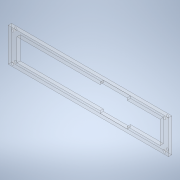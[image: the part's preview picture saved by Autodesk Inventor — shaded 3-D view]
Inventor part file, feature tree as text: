
AUTODESK INVENTOR PART (.ipt)
format: ipt  version: 2021 (Build 250183000, 183)  size: 140,800 bytes
history: native  units: mm
features: extrude x1, sketch x1
ambient origin geometry x8: Origin, YZ Plane, XZ Plane, XY Plane, X Axis, Y Axis, Z Axis, Center Point
bodies: Solid1 (feature_tree)
feature tree (2):
  extrude  "Extrusion1"  Depth=4.0mm
  sketch  "Sketch1"  dims[d0=1.0mm d1=4.0mm d2=110.0mm d3=40.4mm d5=82.0mm d6=4.0mm d7=0.0mm d8=3.0mm d9=5.0mm d10=3.2mm d11=3.0mm d12=5.0mm d13=3.2mm d14=3.0mm d15=5.0mm d16=3.2mm d17=3.0mm d18=5.0mm d19=3.2mm]
